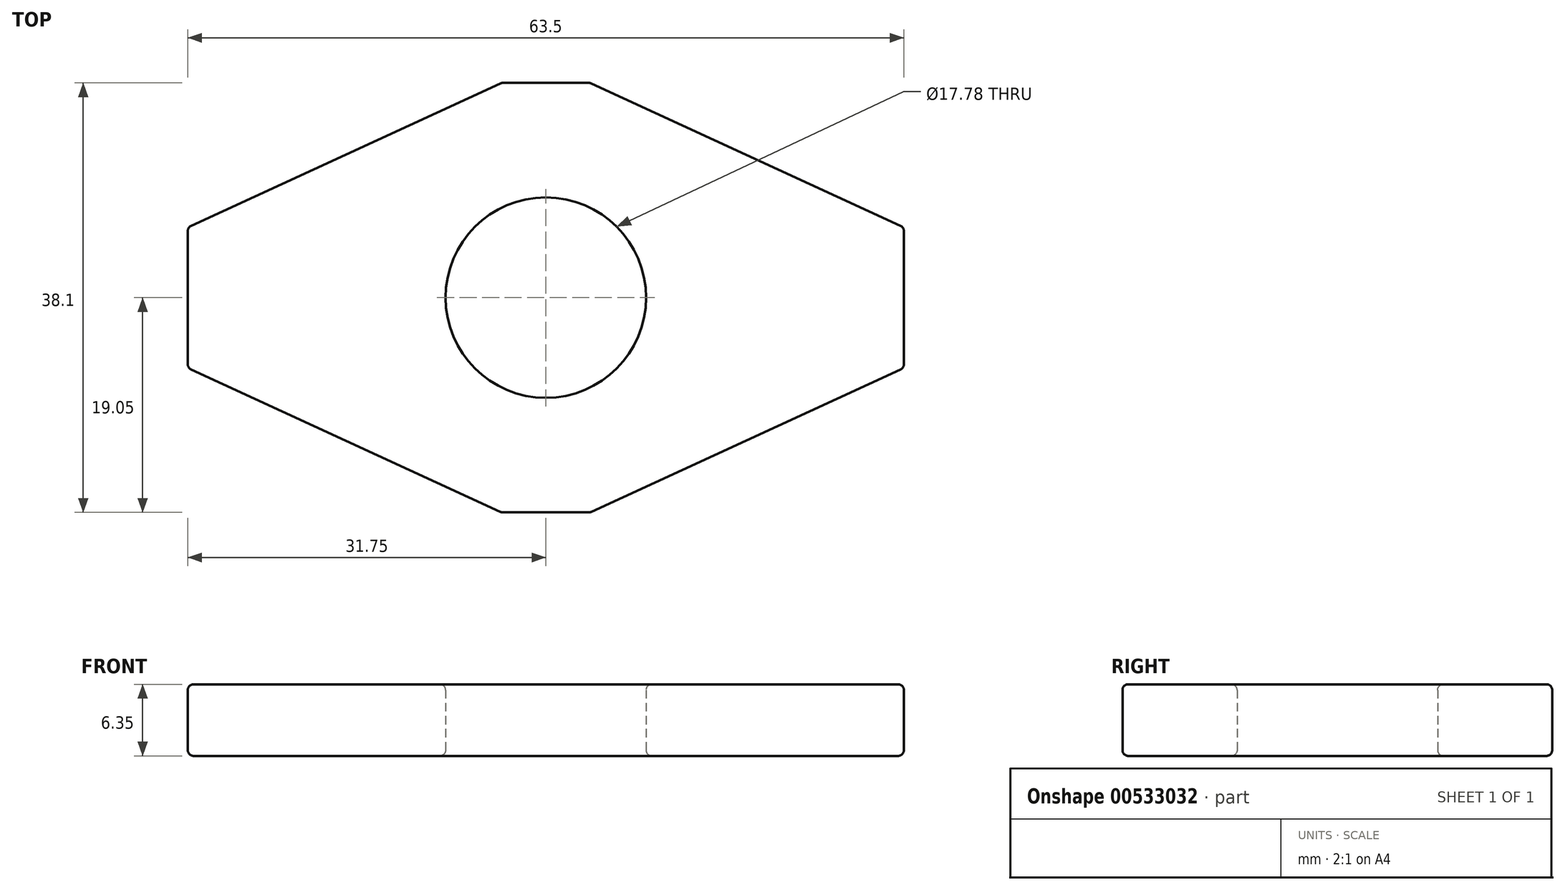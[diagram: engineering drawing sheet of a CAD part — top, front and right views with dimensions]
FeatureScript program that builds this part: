
annotation { "Feature Type Name" : "Feature", "Feature Type Description" : "" }
export const myFeature = defineFeature(function(context is Context, id is Id, definition is map)
    precondition{}
    {
        {
            var Q0;
            Q0=qCreatedBy(makeId("Top.planeOp"),FACE);
            var sketch = newSketch(context, id + "F0", { "sketchPlane" : qUnion([Q0])});
            skLineSegment(sketch, "E0.bottom", {"start": v(-27.83, 0) * mm, "end": v(-35.67, 0) * mm});
            skLineSegment(sketch, "E0.top", {"start": v(-27.83, -38.1) * mm, "end": v(-35.67, -38.1) * mm});
            skLineSegment(sketch, "E0.left", {"start": v(0, -12.81) * mm, "end": v(0, -38.1) * mm});
            skLineSegment(sketch, "E0.right", {"start": v(-63.5, -12.81) * mm, "end": v(-63.5, -25.29) * mm});
            skCircle(sketch, "E1", {"center": v(-31.75, -19.05) * mm, "radius": 8.9 * mm});
            skLineSegment(sketch, "E2", {"start": v(-35.67, 0) * mm, "end": v(-63.5, -12.81) * mm});
            skLineSegment(sketch, "E3.MirrorCS", {"start": v(-27.83, 0) * mm, "end": v(0, -12.81) * mm});
            skLineSegment(sketch, "E4.MirrorCS", {"start": v(-35.67, -38.1) * mm, "end": v(-63.5, -25.29) * mm});
            skLineSegment(sketch, "E5.MirrorCS", {"start": v(-27.83, -38.1) * mm, "end": v(0, -25.29) * mm});
            skPoint(sketch, "E6.orphan", {"position": v(-63.5, 0) * mm});
            skPoint(sketch, "E7.orphan", {"position": v(-63.5, -38.1) * mm});
            skPoint(sketch, "E8.orphan", {"position": v(0, 0) * mm});
            skPoint(sketch, "E9.orphan", {"position": v(0, -19.05) * mm});
            skPoint(sketch, "E10.trimOffspring.end.orphan", {"position": v(-31.75, -38.1) * mm});
            skPoint(sketch, "E11.start.orphan", {"position": v(-63.5, -19.05) * mm});
            skPoint(sketch, "E12.start.orphan", {"position": v(-31.75, 0) * mm});
            skSolve(sketch);
        }
        {
            var Q0;
            Q0=makeQuery(id+"F0.imprint","IMPRINT",FACE,{"disambiguationData":[TD([[makeQuery(id+"F0.imprint","IMPRINT",EDGE,{"derivedFrom":sQuery(id+"F0.wireOp",EDGE,"E0.bottom")}),1.0]])]});
            extrude(context, id + "F1", {"entities" : qUnion([Q0]), "depth" : 6.35 * mm, "offsetDistance" : 25.4 * mm});
        }
        {
            var Q0;
            Q0=makeQuery(id+"F1.opExtrude","SWEPT_FACE",FACE,{"disambiguationData":[OSD([sQuery(id+"F0.wireOp",EDGE,"E4.MirrorCS")])]});
            var Q1;
            Q1=makeQuery(id+"F1.opExtrude","CAP_FACE",FACE,{"disambiguationData":[OSD([sQuery(id+"F0.wireOp",EDGE,"E0.bottom"),sQuery(id+"F0.wireOp",EDGE,"E0.top"),sQuery(id+"F0.wireOp",EDGE,"E0.left"),sQuery(id+"F0.wireOp",EDGE,"E0.right"),sQuery(id+"F0.wireOp",EDGE,"E1"),sQuery(id+"F0.wireOp",EDGE,"E2"),sQuery(id+"F0.wireOp",EDGE,"E3.MirrorCS"),sQuery(id+"F0.wireOp",EDGE,"E4.MirrorCS"),sQuery(id+"F0.wireOp",EDGE,"E5.MirrorCS")])],"isStart":false});
            var Q2;
            Q2=makeQuery(id+"F1.opExtrude","CAP_FACE",FACE,{"disambiguationData":[OSD([sQuery(id+"F0.wireOp",EDGE,"E0.bottom"),sQuery(id+"F0.wireOp",EDGE,"E0.top"),sQuery(id+"F0.wireOp",EDGE,"E0.left"),sQuery(id+"F0.wireOp",EDGE,"E0.right"),sQuery(id+"F0.wireOp",EDGE,"E1"),sQuery(id+"F0.wireOp",EDGE,"E2"),sQuery(id+"F0.wireOp",EDGE,"E3.MirrorCS"),sQuery(id+"F0.wireOp",EDGE,"E4.MirrorCS"),sQuery(id+"F0.wireOp",EDGE,"E5.MirrorCS")])],"isStart":true});
            var Q3;
            Q3=makeQuery(id+"F1.opExtrude","SWEPT_EDGE",EDGE,{"disambiguationData":[OSD([sQuery(id+"F0.wireOp",EDGE,"E0.right"),sQuery(id+"F0.wireOp",EDGE,"E2")])]});
            var Q4;
            Q4=makeQuery(id+"F1.opExtrude","SWEPT_EDGE",EDGE,{"disambiguationData":[OSD([sQuery(id+"F0.wireOp",EDGE,"E0.bottom"),sQuery(id+"F0.wireOp",EDGE,"E2")])]});
            var Q5;
            Q5=makeQuery(id+"F1.opExtrude","SWEPT_EDGE",EDGE,{"disambiguationData":[OSD([sQuery(id+"F0.wireOp",EDGE,"E0.bottom"),sQuery(id+"F0.wireOp",EDGE,"E3.MirrorCS")])]});
            var Q6;
            Q6=makeQuery(id+"F1.opExtrude","SWEPT_EDGE",EDGE,{"disambiguationData":[OSD([sQuery(id+"F0.wireOp",EDGE,"E0.left"),sQuery(id+"F0.wireOp",EDGE,"E3.MirrorCS")])]});
            var Q7;
            Q7=makeQuery(id+"F1.opExtrude","SWEPT_EDGE",EDGE,{"disambiguationData":[OSD([sQuery(id+"F0.wireOp",EDGE,"E0.left"),sQuery(id+"F0.wireOp",EDGE,"E5.MirrorCS")])]});
            var Q8;
            Q8=makeQuery(id+"F1.opExtrude","SWEPT_EDGE",EDGE,{"disambiguationData":[OSD([sQuery(id+"F0.wireOp",EDGE,"E0.top"),sQuery(id+"F0.wireOp",EDGE,"E5.MirrorCS")])]});
            var Q9;
            Q9=makeQuery(id+"F1.opExtrude","SWEPT_EDGE",EDGE,{"disambiguationData":[OSD([sQuery(id+"F0.wireOp",EDGE,"E0.top"),sQuery(id+"F0.wireOp",EDGE,"E4.MirrorCS")])]});
            fillet(context, id + "F2", {"entities" : qUnion([Q0, Q1, Q2, Q3, Q4, Q5, Q6, Q7, Q8, Q9]), "radius" : 0.5 * mm, "tangentPropagation" : true, "allowEdgeOverflow" : false});
        }
    });
